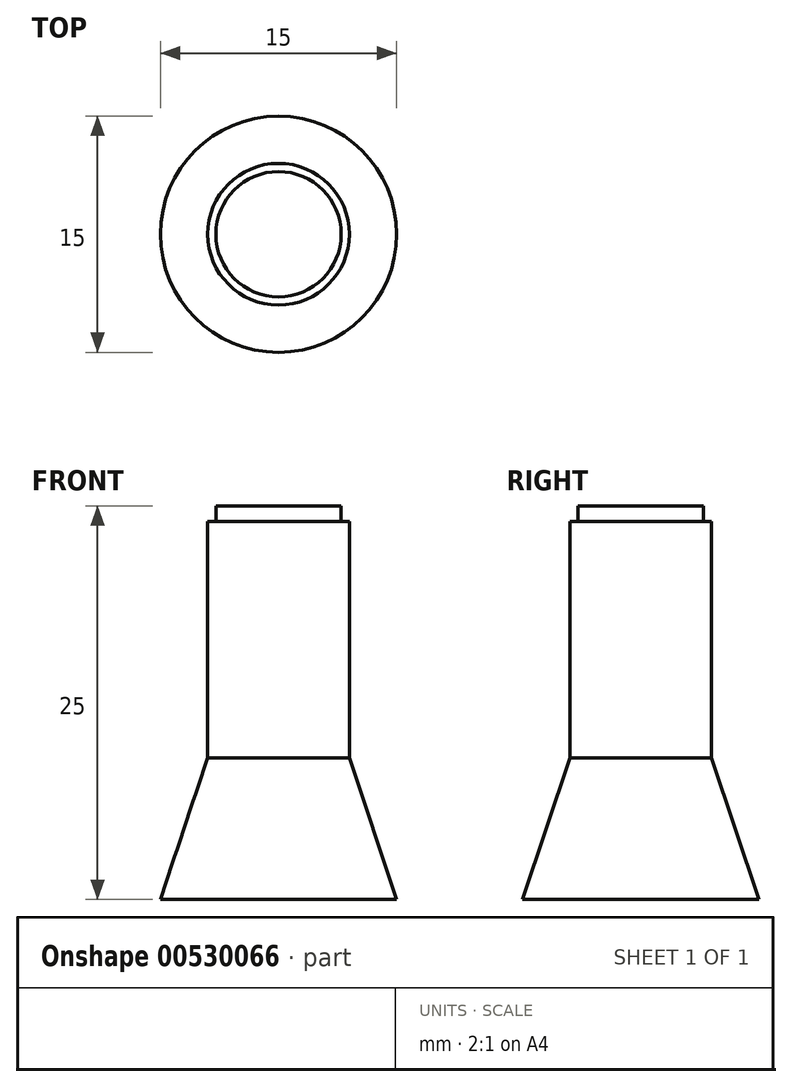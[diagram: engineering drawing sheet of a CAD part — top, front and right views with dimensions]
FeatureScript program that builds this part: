
annotation { "Feature Type Name" : "Feature", "Feature Type Description" : "" }
export const myFeature = defineFeature(function(context is Context, id is Id, definition is map)
    precondition{}
    {
        {
            var Q0;
            Q0=qCreatedBy(makeId("Front.planeOp"),FACE);
            var sketch = newSketch(context, id + "F0", { "sketchPlane" : qUnion([Q0])});
            skLineSegment(sketch, "E0", {"start": v(0, 0) * mm, "end": v(0, 24) * mm});
            skLineSegment(sketch, "E1", {"start": v(0, 24) * mm, "end": v(-4.5, 24) * mm});
            skLineSegment(sketch, "E2", {"start": v(0, 0) * mm, "end": v(-7.5, 0) * mm});
            skLineSegment(sketch, "E3", {"start": v(-4.5, 24) * mm, "end": v(-4.5, 9) * mm});
            skLineSegment(sketch, "E4", {"start": v(-4.5, 9) * mm, "end": v(-7.5, 0) * mm});
            skSolve(sketch);
        }
        {
            var Q0;
            {var subQ0=sQuery(id+"F0.wireOp",EDGE,"E2");Q0=makeQuery(id+"F0.imprint","IMPRINT",FACE,{"disambiguationData":[TD([[makeQuery(id+"F0.imprint","IMPRINT",EDGE,{"derivedFrom":subQ0}),-1.0]])]});}
            var Q1;
            Q1=makeQuery(id+"F0.imprint","IMPRINT",FACE,{"disambiguationData":[TD([[makeQuery(id+"F0.imprint","IMPRINT",EDGE,{"derivedFrom":sQuery(id+"F0.wireOp",EDGE,"E0")}),1.0]])]});
            var Q2;
            Q2=sQuery(id+"F0.wireOp",EDGE,"E0");
            revolve(context, id + "F1", {"entities" : qUnion([Q0, Q1]), "axis" : qUnion([Q2]), "revolveType" : RevolveType.FULL});
        }
        {
            var Q0;
            Q0=qCreatedBy(makeId("Front.planeOp"),FACE);
            var sketch = newSketch(context, id + "F2", { "sketchPlane" : qUnion([Q0])});
            skLineSegment(sketch, "E5", {"start": v(0, 0) * mm, "end": v(0, 25) * mm});
            skLineSegment(sketch, "E6", {"start": v(-3.98, 25) * mm, "end": v(-3.98, 0) * mm});
            skLineSegment(sketch, "E7", {"start": v(-3.98, 25) * mm, "end": v(0, 25) * mm});
            skLineSegment(sketch, "E8", {"start": v(0, 0) * mm, "end": v(-3.98, 0) * mm});
            skSolve(sketch);
        }
        {
            var Q0;
            Q0 = qSketchRegion(id + "F2", true);
            var Q1;
            Q1=sQuery(id+"F2.wireOp",EDGE,"E5");
            revolve(context, id + "F3", {"operationType" : NewBodyOperationType.ADD, "entities" : qUnion([Q0]), "axis" : qUnion([Q1]), "revolveType" : RevolveType.FULL});
        }
    });
